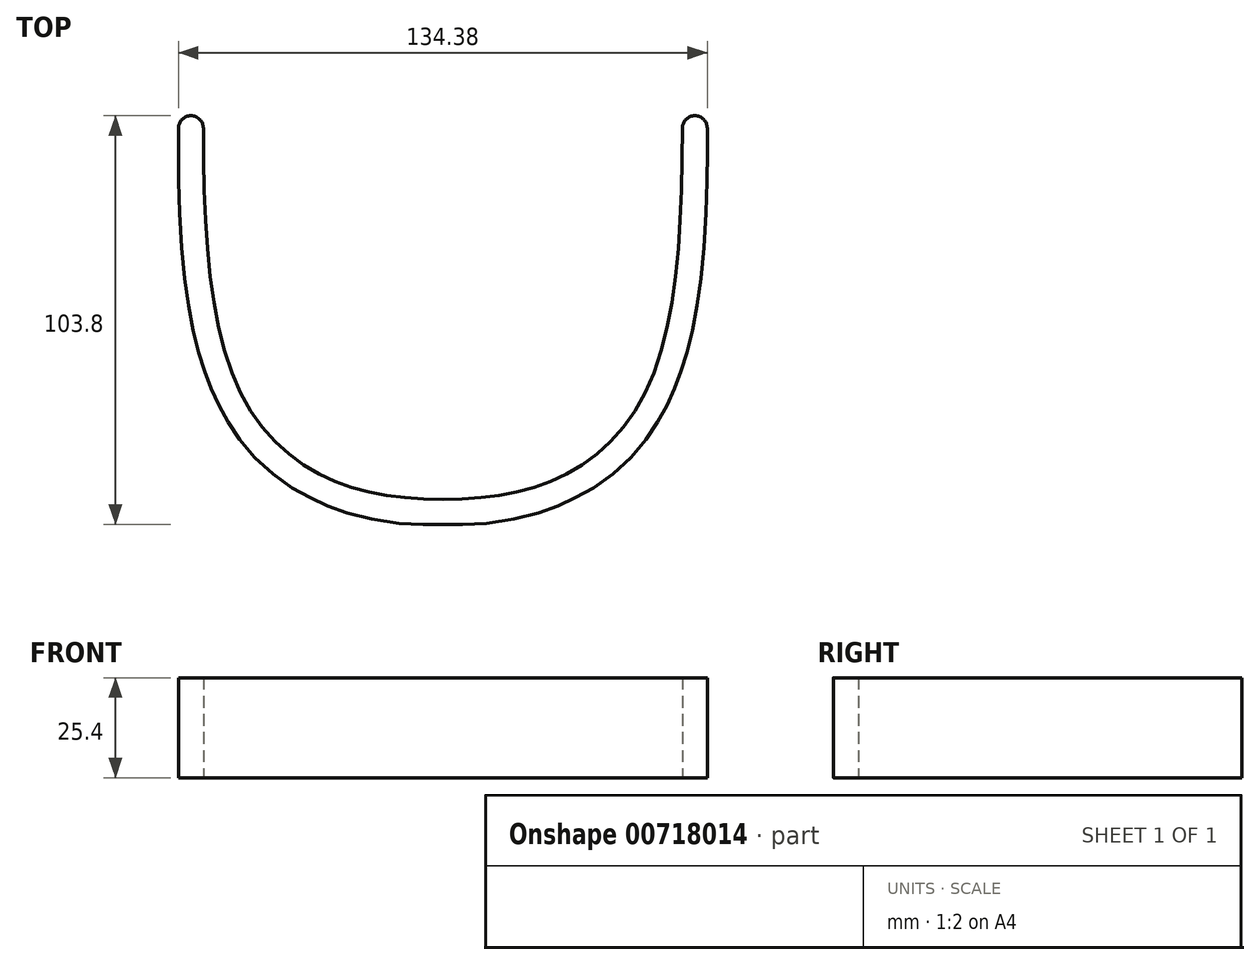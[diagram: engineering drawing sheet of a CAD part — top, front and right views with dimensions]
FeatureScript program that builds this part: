
annotation { "Feature Type Name" : "Feature", "Feature Type Description" : "" }
export const myFeature = defineFeature(function(context is Context, id is Id, definition is map)
    precondition{}
    {
        {
            var Q0;
            Q0=qCreatedBy(makeId("Top.planeOp"),FACE);
            var sketch = newSketch(context, id + "F0", { "sketchPlane" : qUnion([Q0])});
            skFitSpline(sketch, "E0", {"points": [v(0, 0) * mm, v(29.58, 5.48) * mm, v(52.06, 28.5) * mm, v(60.84, 94.26) * mm], "startDerivative": vector(113.74, 0) * mm, "endDerivative": vector(0, 185.14) * mm});
            skLineSegment(sketch, "E1", {"start": v(0, 0) * mm, "end": v(0, 33.24) * mm, "construction": true});
            skFitSpline(sketch, "E2.MirrorCS", {"points": [v(0, 0) * mm, v(-29.58, 5.48) * mm, v(-52.06, 28.5) * mm, v(-60.84, 94.26) * mm], "startDerivative": vector(-113.74, 0) * mm, "endDerivative": vector(0, 185.14) * mm});
            skFitSpline(sketch, "E3.0", {"points": [v(0, -6.35) * mm, v(4.96, -6.35) * mm, v(12.27, -5.97) * mm, v(21.73, -4.15) * mm, v(27.5, -2.35) * mm, v(32, -0.44) * mm, v(36.4, 1.79) * mm, v(41.67, 5.2) * mm, v(47.5, 10.33) * mm, v(51.8, 15.47) * mm, v(54.85, 20.1) * mm, v(56.92, 23.84) * mm, v(58.77, 27.83) * mm, v(60.36, 32.02) * mm, v(61.74, 36.4) * mm, v(63.3, 42.48) * mm, v(64.81, 50.5) * mm, v(66.03, 60.74) * mm, v(67, 75.07) * mm, v(67.19, 86.48) * mm, v(67.19, 94.26) * mm]});
            skFitSpline(sketch, "E3.1", {"points": [v(0, -6.35) * mm, v(-4.96, -6.35) * mm, v(-12.27, -5.97) * mm, v(-21.73, -4.15) * mm, v(-27.5, -2.35) * mm, v(-32, -0.44) * mm, v(-36.4, 1.79) * mm, v(-41.67, 5.2) * mm, v(-47.5, 10.33) * mm, v(-51.8, 15.47) * mm, v(-54.85, 20.1) * mm, v(-56.92, 23.84) * mm, v(-58.77, 27.83) * mm, v(-60.36, 32.02) * mm, v(-61.74, 36.4) * mm, v(-63.3, 42.48) * mm, v(-64.81, 50.5) * mm, v(-66.03, 60.74) * mm, v(-67, 75.07) * mm, v(-67.19, 86.48) * mm, v(-67.19, 94.26) * mm]});
            skArc(sketch, "E4", {"start": v(-67.19, 94.26) * mm, "mid": v(-64.01, 97.44) * mm, "end": v(-60.84, 94.26) * mm});
            skArc(sketch, "E5", {"start": v(67.19, 94.26) * mm, "mid": v(64.01, 97.44) * mm, "end": v(60.84, 94.26) * mm});
            skSolve(sketch);
        }
        {
            var Q0;
            Q0=makeQuery(id+"F0.imprint","IMPRINT",FACE,{"disambiguationData":[TD([[makeQuery(id+"F0.imprint","IMPRINT",EDGE,{"derivedFrom":sQuery(id+"F0.wireOp",EDGE,"E0")}),-1.0]])]});
            extrude(context, id + "F1", {"entities" : qUnion([Q0]), "depth" : 25.4 * mm, "offsetDistance" : 25.4 * mm});
        }
    });
